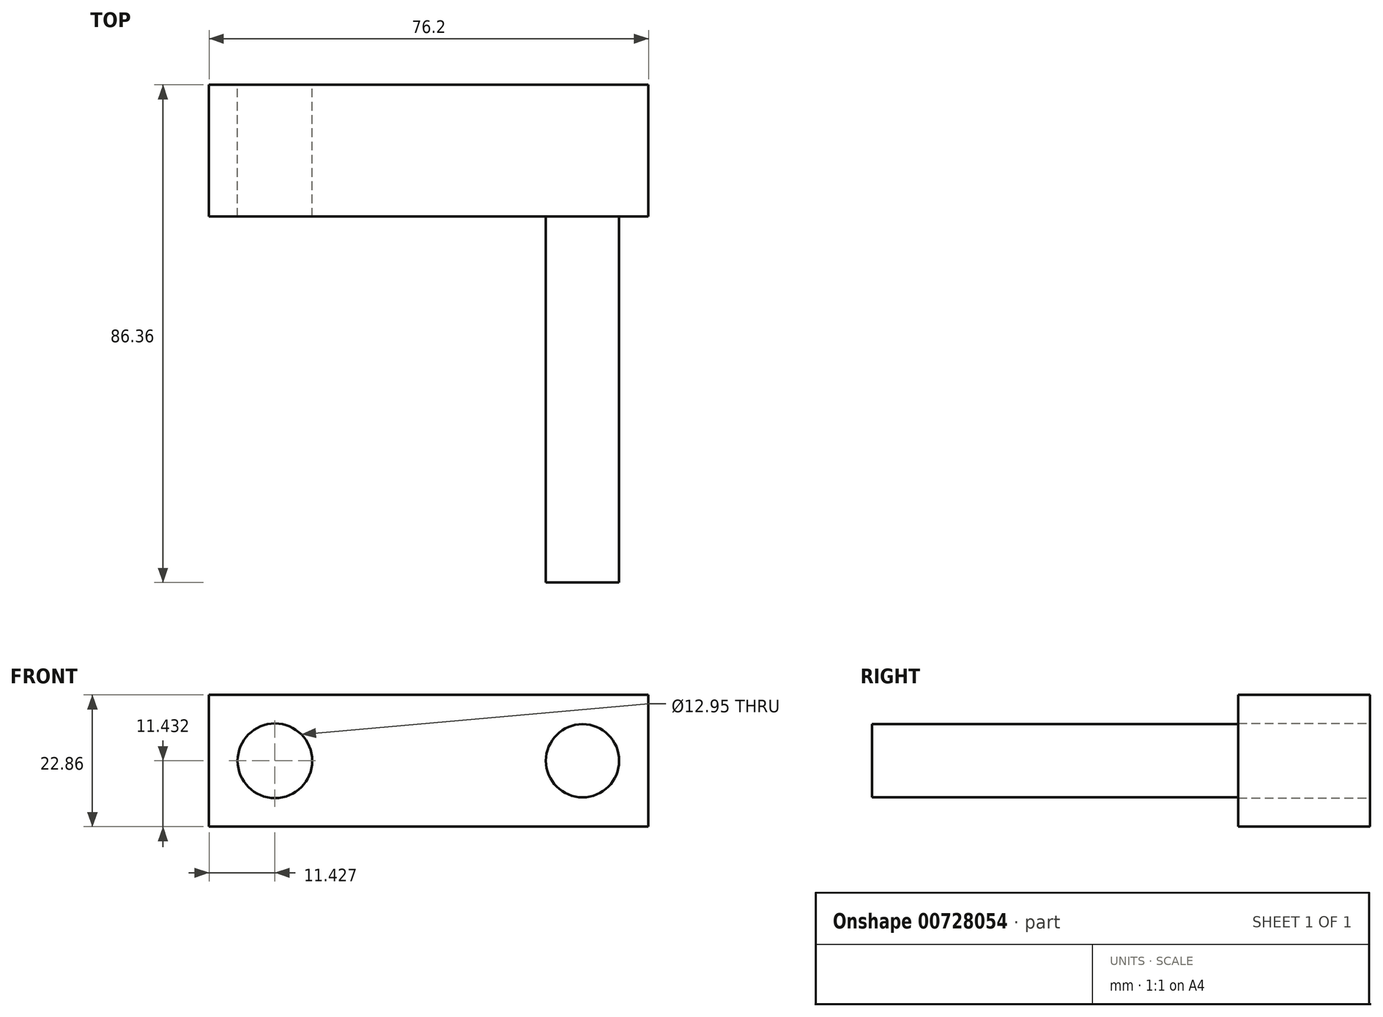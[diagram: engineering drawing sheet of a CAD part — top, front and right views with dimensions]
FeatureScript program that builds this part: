
annotation { "Feature Type Name" : "Feature", "Feature Type Description" : "" }
export const myFeature = defineFeature(function(context is Context, id is Id, definition is map)
    precondition{}
    {
        {
            var Q0;
            Q0=qCreatedBy(makeId("Front.planeOp"),FACE);
            var sketch = newSketch(context, id + "F0", { "sketchPlane" : qUnion([Q0])});
            skCircle(sketch, "E0", {"center": v(-39.91, 38.62) * mm, "radius": 6.48 * mm});
            skLineSegment(sketch, "E1.bottom", {"start": v(24.86, 50.05) * mm, "end": v(-51.34, 50.05) * mm});
            skLineSegment(sketch, "E1.top", {"start": v(24.86, 27.2) * mm, "end": v(-51.34, 27.2) * mm});
            skLineSegment(sketch, "E1.left", {"start": v(24.86, 50.05) * mm, "end": v(24.86, 27.2) * mm});
            skLineSegment(sketch, "E1.right", {"start": v(-51.34, 50.05) * mm, "end": v(-51.34, 27.2) * mm});
            skSolve(sketch);
        }
        {
            var Q0;
            Q0=makeQuery(id+"F0.imprint","IMPRINT",FACE,{"disambiguationData":[TD([[makeQuery(id+"F0.imprint","IMPRINT",EDGE,{"derivedFrom":sQuery(id+"F0.wireOp",EDGE,"E0")}),-1.0]])]});
            extrude(context, id + "F1", {"entities" : qUnion([Q0]), "depth" : 22.86 * mm, "offsetDistance" : 25.4 * mm});
        }
        {
            var Q0;
            Q0=makeQuery(id+"F1.opExtrude","CAP_FACE",FACE,{"disambiguationData":[OSD([sQuery(id+"F0.wireOp",EDGE,"E0"),sQuery(id+"F0.wireOp",EDGE,"E1.bottom"),sQuery(id+"F0.wireOp",EDGE,"E1.top"),sQuery(id+"F0.wireOp",EDGE,"E1.left"),sQuery(id+"F0.wireOp",EDGE,"E1.right")])],"isStart":false});
            var sketch = newSketch(context, id + "F2", { "sketchPlane" : qUnion([Q0])});
            skCircle(sketch, "E2", {"center": v(13.43, 38.62) * mm, "radius": 6.35 * mm});
            skSolve(sketch);
        }
        {
            var Q0;
            Q0=makeQuery(id+"F2.imprint","IMPRINT",FACE,{"disambiguationData":[TD([[makeQuery(id+"F2.imprint","IMPRINT",EDGE,{"derivedFrom":sQuery(id+"F2.wireOp",EDGE,"E2")}),1.0]])]});
            extrude(context, id + "F3", {"entities" : qUnion([Q0]), "operationType" : NewBodyOperationType.ADD, "depth" : 63.5 * mm, "offsetDistance" : 25.4 * mm});
        }
    });
